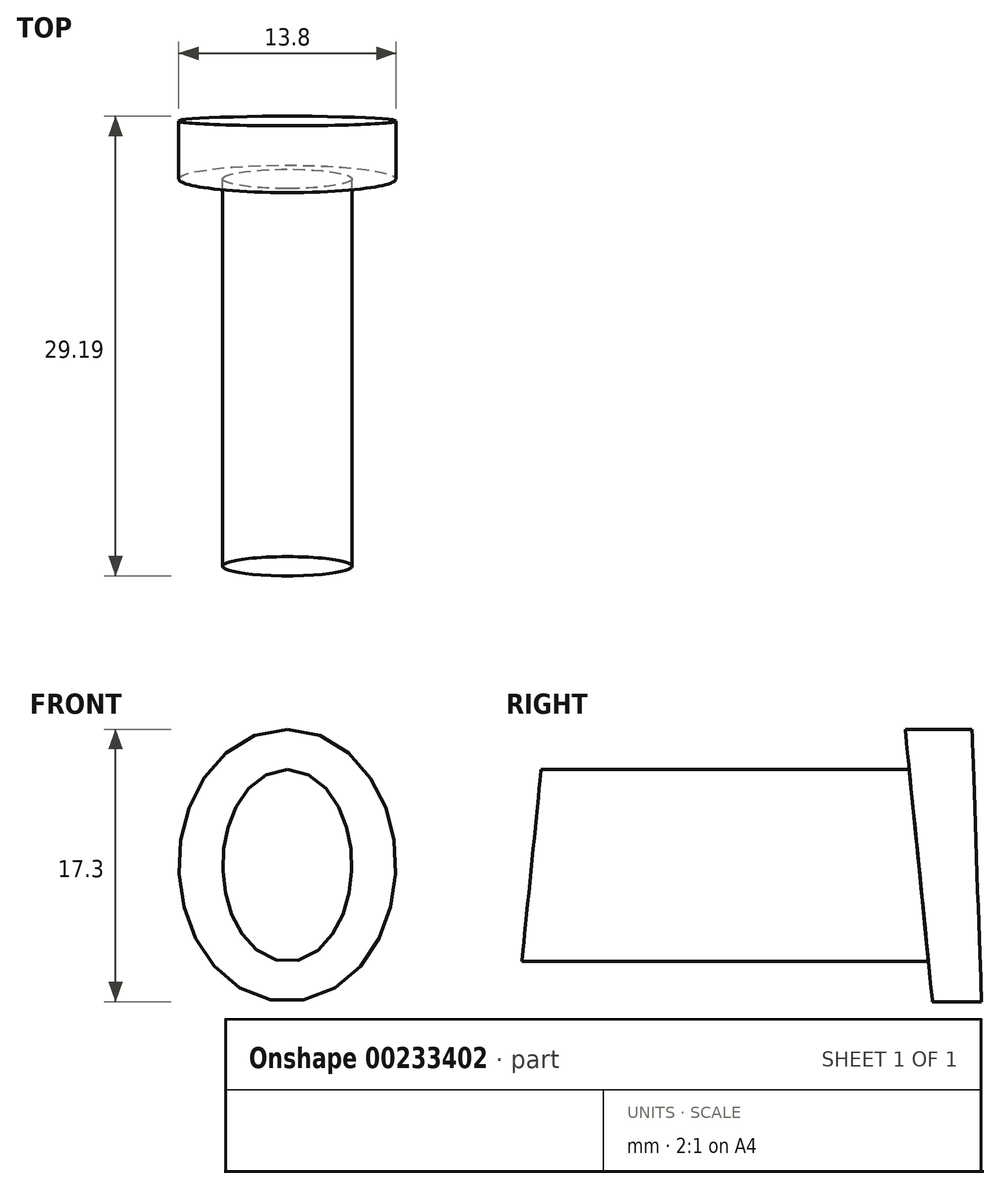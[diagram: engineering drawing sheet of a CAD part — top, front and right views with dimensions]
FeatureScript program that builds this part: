
annotation { "Feature Type Name" : "Feature", "Feature Type Description" : "" }
export const myFeature = defineFeature(function(context is Context, id is Id, definition is map)
    precondition{}
    {
        {
            var Q0;
            Q0=qCreatedBy(makeId("Front.planeOp"),FACE);
            var sketch = newSketch(context, id + "F0", { "sketchPlane" : qUnion([Q0])});
            skEllipse(sketch, "E0", {"center": v(0, 0) * mm, "majorRadius": 6.5 * mm, "minorRadius": 4.5 * mm, "majorAxis": v(0, 1), "construction": true});
            skPoint(sketch, "E1", {"position": v(0, 6.5) * mm});
            skPoint(sketch, "E2", {"position": v(0, -6.5) * mm});
            skPoint(sketch, "E3", {"position": v(4.5, 0) * mm});
            skPoint(sketch, "E4", {"position": v(-4.5, 0) * mm});
            skEllipse(sketch, "E5", {"center": v(0, 0) * mm, "majorRadius": 6.1 * mm, "minorRadius": 4.1 * mm, "majorAxis": v(0, 1)});
            skPoint(sketch, "E6", {"position": v(4.1, 0) * mm});
            skPoint(sketch, "E7", {"position": v(0, 6.1) * mm});
            skSolve(sketch);
        }
        {
            var Q0;
            Q0 = qSketchRegion(id + "F0", true);
            extrude(context, id + "F1", {"entities" : qUnion([Q0]), "depth" : (25.9 / 2) * mm});
        }
        {
            var Q0;
            Q0=qCreatedBy(makeId("Right.planeOp"),FACE);
            var sketch = newSketch(context, id + "F2", { "sketchPlane" : qUnion([Q0])});
            skLineSegment(sketch, "E8", {"start": v(-11.65, 6.5) * mm, "end": v(-12.95, -6.5) * mm});
            skLineSegment(sketch, "E9", {"start": v(-11.65, 6.5) * mm, "end": v(-17.1, 6.5) * mm});
            skLineSegment(sketch, "E10", {"start": v(-17.1, 6.5) * mm, "end": v(-17.1, -6.5) * mm});
            skLineSegment(sketch, "E11", {"start": v(-17.1, -6.5) * mm, "end": v(-12.95, -6.5) * mm});
            skSolve(sketch);
        }
        {
            var Q0;
            Q0 = qSketchRegion(id + "F2", true);
            extrude(context, id + "F3", {"entities" : qUnion([Q0]), "operationType" : NewBodyOperationType.REMOVE, "endBound" : BoundingType.THROUGH_ALL, "oppositeDirection" : true, "depth" : 25 * mm, "hasSecondDirection" : true, "secondDirectionBound" : SecondDirectionBoundingType.THROUGH_ALL, "secondDirectionOppositeDirection" : false, "secondDirectionDepth" : 25 * mm});
        }
        {
            var Q0;
            Q0=makeQuery(id+"F1.opExtrude","SWEPT_BODY",BODY,{"disambiguationData":[OSD([sQuery(id+"F0.wireOp",EDGE,"E5")])]});
            var Q1;
            Q1=qCreatedBy(makeId("Front.planeOp"),FACE);
            mirror(context, id + "F4", {"operationType" : NewBodyOperationType.ADD, "entities" : qUnion([Q0]), "mirrorPlane" : qUnion([Q1])});
        }
        {
            var Q0;
            Q0=makeQuery(id+"F4.opPattern","COPY",FACE,{"derivedFrom":makeQuery(id+"F3.boolean.opBoolean","COPY",FACE,{"derivedFrom":makeQuery(id+"F3.opExtrude","SWEPT_FACE",FACE,{"disambiguationData":[OSD([sQuery(id+"F2.wireOp",EDGE,"E8")])]})}),"instanceName":"1"});
            var sketch = newSketch(context, id + "F5", { "sketchPlane" : qUnion([Q0])});
            skEllipse(sketch, "E12", {"center": v(0, -1.22) * mm, "majorRadius": 10.73 * mm, "minorRadius": 8.7 * mm, "majorAxis": v(0, -1)});
            skLineSegment(sketch, "E13", {"start": v(0, 4.9) * mm, "end": v(0, -7.35) * mm, "construction": true});
            skPoint(sketch, "E14", {"position": v(0, 9.9) * mm});
            skPoint(sketch, "E15", {"position": v(9.1, -1.22) * mm});
            skPoint(sketch, "E16", {"position": v(4.1, -1.22) * mm});
            skSolve(sketch);
        }
        {
            var Q0;
            Q0 = qSketchRegion(id + "F5", true);
            extrude(context, id + "F6", {"entities" : qUnion([Q0]), "operationType" : NewBodyOperationType.ADD, "depth" : 6 * mm});
        }
        {
            var Q0;
            Q0=qCreatedBy(makeId("Front.planeOp"),FACE);
            var sketch = newSketch(context, id + "F7", { "sketchPlane" : qUnion([Q0])});
            skEllipse(sketch, "E17", {"center": v(0, 0) * mm, "majorRadius": 8.65 * mm, "minorRadius": 6.9 * mm, "majorAxis": v(0, 1)});
            skPoint(sketch, "E18", {"position": v(0, 8.5) * mm});
            skPoint(sketch, "E19", {"position": v(-6.9, 0) * mm});
            skSolve(sketch);
        }
        {
            var Q0;
            Q0 = qSketchRegion(id + "F7", true);
            extrude(context, id + "F8", {"entities" : qUnion([Q0]), "operationType" : NewBodyOperationType.INTERSECT, "endBound" : BoundingType.THROUGH_ALL, "depth" : 25 * mm, "hasSecondDirection" : true, "secondDirectionBound" : SecondDirectionBoundingType.THROUGH_ALL, "secondDirectionOppositeDirection" : true, "secondDirectionDepth" : 25 * mm});
        }
        {
            var Q0;
            Q0=qCreatedBy(makeId("Right.planeOp"),FACE);
            var sketch = newSketch(context, id + "F9", { "sketchPlane" : qUnion([Q0])});
            skLineSegment(sketch, "E20.bottom", {"start": v(15.6, 11.08) * mm, "end": v(22.37, 11.08) * mm});
            skLineSegment(sketch, "E20.top", {"start": v(16.37, -11.08) * mm, "end": v(22.37, -11.08) * mm});
            skLineSegment(sketch, "E20.right", {"start": v(22.37, 11.08) * mm, "end": v(22.37, -11.08) * mm});
            skPoint(sketch, "E21", {"position": v(22.37, 0) * mm});
            skLineSegment(sketch, "E22", {"start": v(15.6, 11.08) * mm, "end": v(16.37, -11.08) * mm});
            skSolve(sketch);
        }
        {
            var Q0;
            Q0 = qSketchRegion(id + "F9", true);
            extrude(context, id + "F10", {"entities" : qUnion([Q0]), "operationType" : NewBodyOperationType.REMOVE, "endBound" : BoundingType.THROUGH_ALL, "oppositeDirection" : true, "depth" : 25 * mm, "hasSecondDirection" : true, "secondDirectionBound" : SecondDirectionBoundingType.THROUGH_ALL, "secondDirectionOppositeDirection" : false, "secondDirectionDepth" : 25 * mm});
        }
    });
